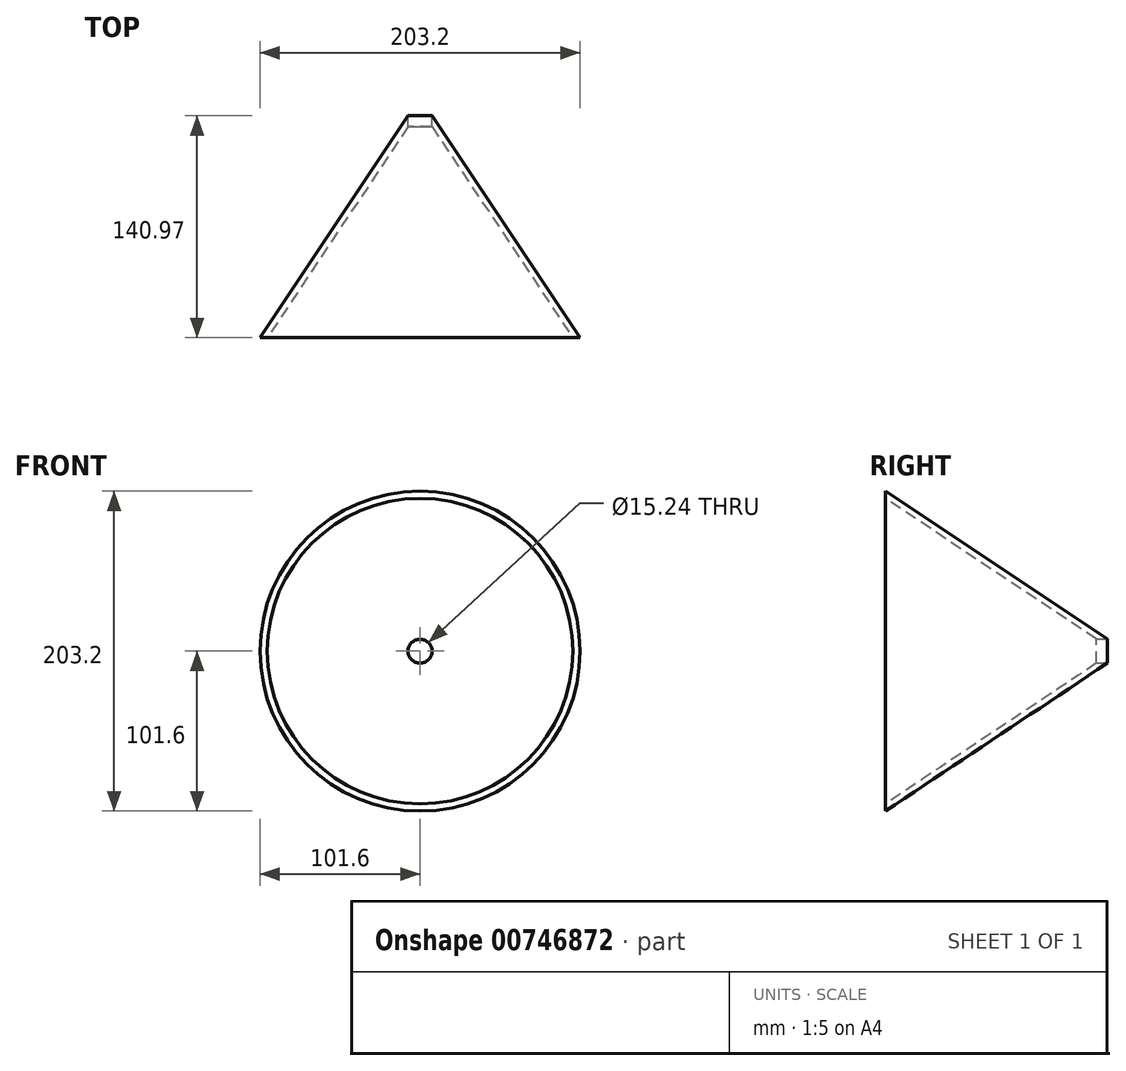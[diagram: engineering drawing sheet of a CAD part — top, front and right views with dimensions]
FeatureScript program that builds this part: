
annotation { "Feature Type Name" : "Feature", "Feature Type Description" : "" }
export const myFeature = defineFeature(function(context is Context, id is Id, definition is map)
    precondition{}
    {
        {
            var Q0;
            Q0=qCreatedBy(makeId("Top.planeOp"),FACE);
            var sketch = newSketch(context, id + "F0", { "sketchPlane" : qUnion([Q0])});
            skLineSegment(sketch, "E0", {"start": v(0, 0) * mm, "end": v(0, 152.4) * mm});
            skLineSegment(sketch, "E1", {"start": v(0, 0) * mm, "end": v(101.6, 0) * mm});
            skLineSegment(sketch, "E2", {"start": v(0, 152.4) * mm, "end": v(101.6, 0) * mm});
            skSolve(sketch);
        }
        {
            var Q0;
            Q0=makeQuery(id+"F0.imprint","IMPRINT",FACE,{"disambiguationData":[TD([[makeQuery(id+"F0.imprint","IMPRINT",EDGE,{"derivedFrom":sQuery(id+"F0.wireOp",EDGE,"E0")}),-1.0]])]});
            var Q1;
            Q1=sQuery(id+"F0.wireOp",EDGE,"E0");
            revolve(context, id + "F1", {"surfaceOperationType" : NewSurfaceOperationType.NEW, "entities" : qUnion([Q0]), "axis" : qUnion([Q1]), "revolveType" : RevolveType.FULL});
        }
        {
            var Q0;
            Q0=makeQuery(id+"F1.opRevolve","SWEPT_FACE",FACE,{"disambiguationData":[OSD([sQuery(id+"F0.wireOp",EDGE,"E1")])]});
            cPlane(context, id + "F2", {"entities" : qUnion([Q0]), "cplaneType" : CPlaneType.OFFSET, "offset" : 152.4 * mm, "oppositeDirection" : true, "width" : 152.4 * mm, "height" : 152.4 * mm});
        }
        {
            var Q0;
            Q0=makeQuery(id+"F1.opRevolve","SWEPT_FACE",FACE,{"disambiguationData":[OSD([sQuery(id+"F0.wireOp",EDGE,"E1")])]});
            shell(context, id + "F3", {"entities" : qUnion([Q0]), "thickness" : 3.8 * mm});
        }
        {
            var Q0;
            Q0=qCreatedBy(id+"F2.planeOp",FACE);
            var sketch = newSketch(context, id + "F4", { "sketchPlane" : qUnion([Q0])});
            skCircle(sketch, "E3", {"center": v(0, 0) * mm, "radius": 7.62 * mm});
            skSolve(sketch);
        }
        {
            var Q0;
            Q0=makeQuery(id+"F4.imprint","IMPRINT",FACE,{"disambiguationData":[TD([[makeQuery(id+"F4.imprint","IMPRINT",EDGE,{"derivedFrom":sQuery(id+"F4.wireOp",EDGE,"E3")}),1.0]])]});
            extrude(context, id + "F5", {"entities" : qUnion([Q0]), "operationType" : NewBodyOperationType.REMOVE, "depth" : 33.02 * mm, "offsetDistance" : 25.4 * mm});
        }
    });
